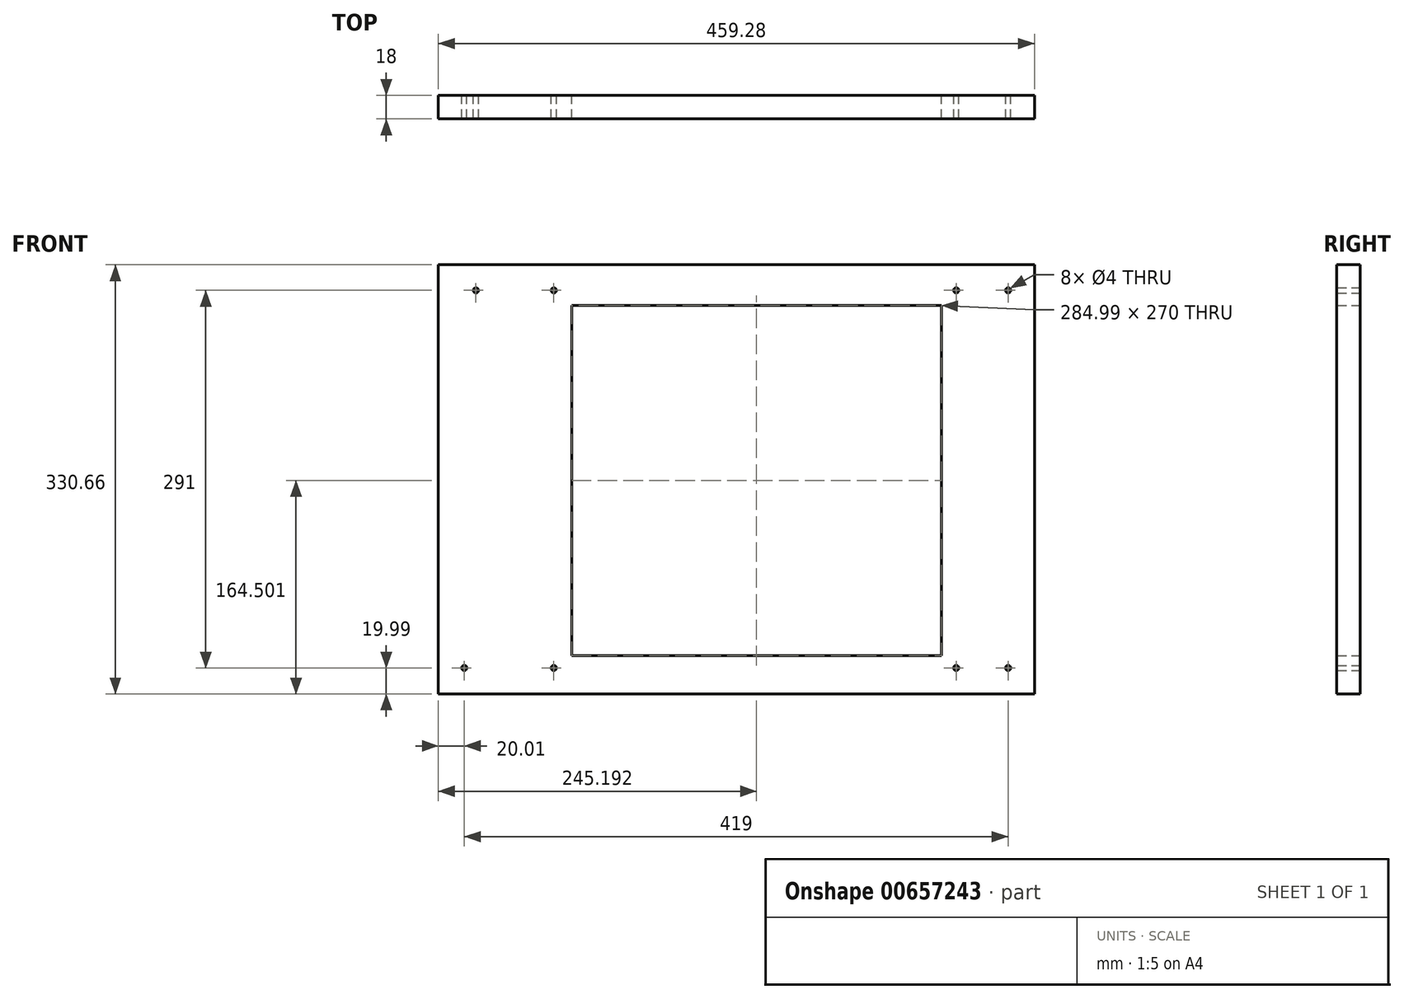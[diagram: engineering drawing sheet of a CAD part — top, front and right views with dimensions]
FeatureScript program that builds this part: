
annotation { "Feature Type Name" : "Feature", "Feature Type Description" : "" }
export const myFeature = defineFeature(function(context is Context, id is Id, definition is map)
    precondition{}
    {
        {
            var Q0;
            Q0=qCreatedBy(makeId("Front.planeOp"),FACE);
            var sketch = newSketch(context, id + "F0", { "sketchPlane" : qUnion([Q0])});
            skCircle(sketch, "E0", {"center": v(-167.48, 160) * mm, "radius": 2 * mm});
            skCircle(sketch, "E1", {"center": v(142.52, 160) * mm, "radius": 2 * mm});
            skCircle(sketch, "E2", {"center": v(142.52, -131) * mm, "radius": 2 * mm});
            skCircle(sketch, "E3", {"center": v(-167.48, -131) * mm, "radius": 2 * mm});
            skCircle(sketch, "E4", {"center": v(182.52, 160) * mm, "radius": 2 * mm});
            skCircle(sketch, "E5", {"center": v(182.52, -131) * mm, "radius": 2 * mm});
            skCircle(sketch, "E6", {"center": v(-227.48, 160) * mm, "radius": 2 * mm});
            skCircle(sketch, "E7", {"center": v(-236.48, -131) * mm, "radius": 2 * mm});
            skLineSegment(sketch, "E8.bottom", {"start": v(-256.49, -150.99) * mm, "end": v(202.79, -150.99) * mm});
            skLineSegment(sketch, "E8.top", {"start": v(-256.49, 179.67) * mm, "end": v(202.79, 179.67) * mm});
            skLineSegment(sketch, "E8.left", {"start": v(-256.49, -150.99) * mm, "end": v(-256.49, 179.67) * mm});
            skLineSegment(sketch, "E8.right", {"start": v(202.79, -150.99) * mm, "end": v(202.79, 179.67) * mm});
            skLineSegment(sketch, "E9.bottom", {"start": v(-153.8, 148.51) * mm, "end": v(131.2, 148.51) * mm});
            skLineSegment(sketch, "E9.top", {"start": v(-153.8, -121.49) * mm, "end": v(131.2, -121.49) * mm});
            skLineSegment(sketch, "E9.left", {"start": v(-153.8, 148.51) * mm, "end": v(-153.8, -121.49) * mm});
            skLineSegment(sketch, "E9.right", {"start": v(131.2, 148.51) * mm, "end": v(131.2, -121.49) * mm});
            skSolve(sketch);
        }
        {
            var Q0;
            Q0 = qSketchRegion(id + "F0", true);
            extrude(context, id + "F1", {"entities" : qUnion([Q0]), "depth" : 18 * mm, "offsetDistance" : 25 * mm});
        }
    });
